# Revit family: MEP-2006
name_source: partatom
category: Aparatos sanitarios
units: mm (PartAtom-declared; Revit-internal decimal feet)

## family parameters
Compartido = No
Corte con vacíos al cargar = No
Cota de conector redondo = Diámetro de uso
Número OmniClass = 23.45.00.00
Punto de cálculo de habitación = No
Se basa en plano de trabajo = No
Siempre vertical = Sí
Tipo de pieza = Normal
Título OmniClass = Sanitary, Laundry, and Cleaning Equipment

## types (1)
- MEP-2006
    Brass Chromed = Brass
    Comentarios de tipo = Mezcladora para lavabo sin desagüe de push, instalación de 8" a 12" con valvex l izquierdo por compresión.
    Descripción = Mezcladora de 8" a 12" sin Desagüe de Push
    Elevación por defecto = 0"
    Fabricante = HELVEX
    Installation Adjustment = 8", 10" ó 12"
    Installation Thread = ½" - 14 NPSM
    Max. Working Pressure = 85.3 psi
    Min. Working Pressure = 3.5 psi
    Modelo = MEP-2006
    Total Height = 4"
    Total Length = 7"
    Total Width = 12"

## geometry (parser evidence)
native form markers: Sweep x3
no freeform markers — native parametric forms only
